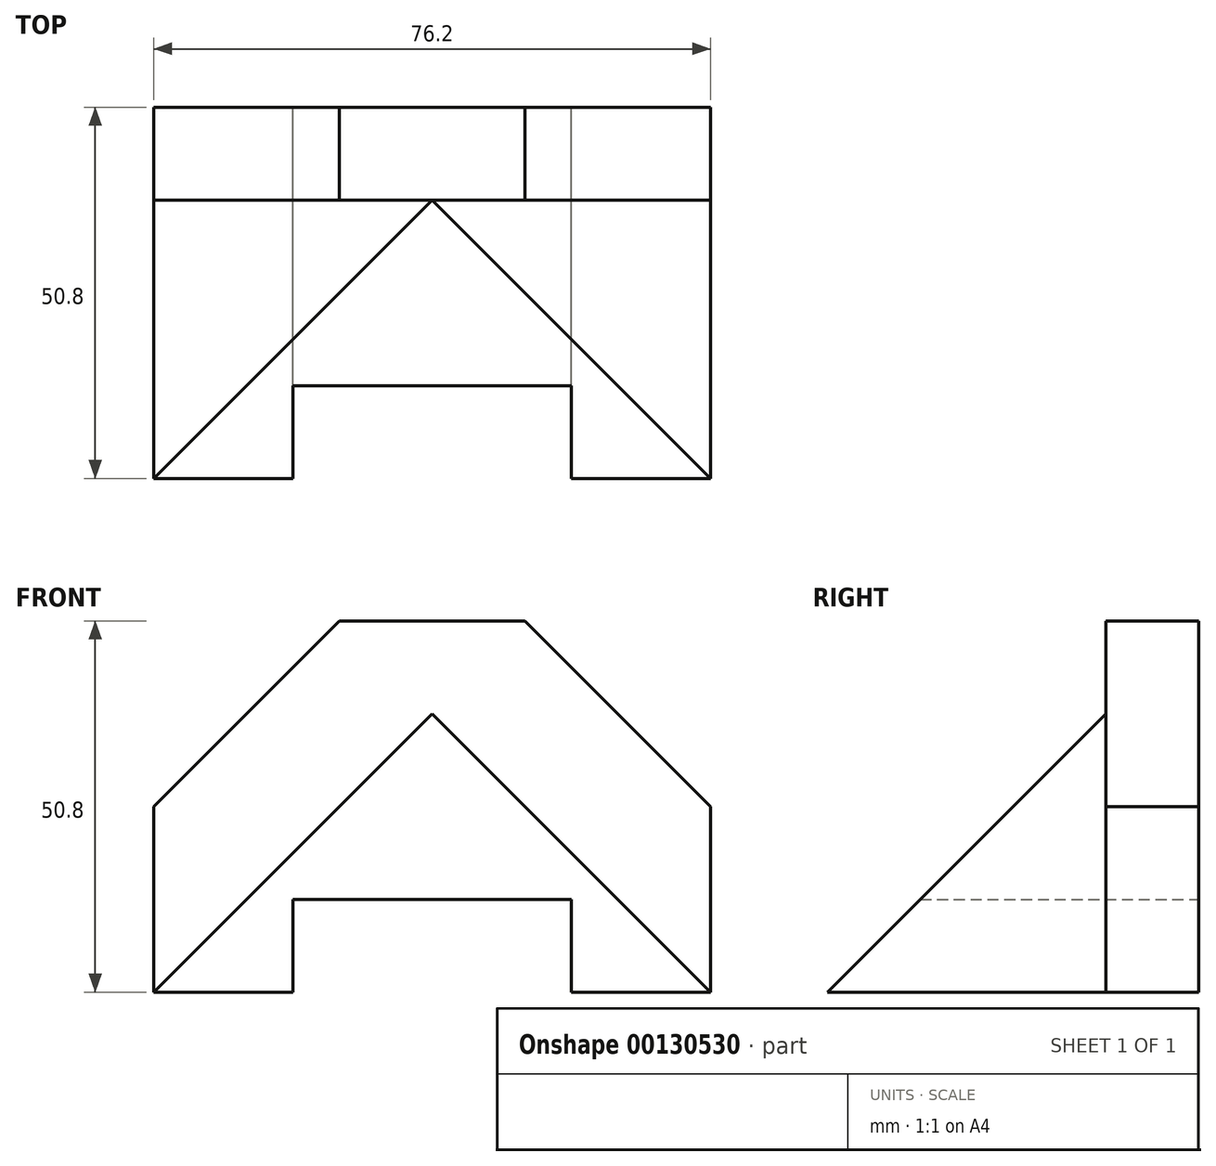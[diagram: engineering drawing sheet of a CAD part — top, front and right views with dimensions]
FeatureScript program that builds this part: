
annotation { "Feature Type Name" : "Feature", "Feature Type Description" : "" }
export const myFeature = defineFeature(function(context is Context, id is Id, definition is map)
    precondition{}
    {
        {
            var Q0;
            Q0=qCreatedBy(makeId("Front.planeOp"),FACE);
            var sketch = newSketch(context, id + "F0", { "sketchPlane" : qUnion([Q0])});
            skLineSegment(sketch, "E0", {"start": v(0, 0) * mm, "end": v(-38.1, 0) * mm});
            skLineSegment(sketch, "E1", {"start": v(-38.1, 0) * mm, "end": v(-38.1, 25.4) * mm});
            skLineSegment(sketch, "E2", {"start": v(-38.1, 25.4) * mm, "end": v(-12.7, 50.8) * mm});
            skLineSegment(sketch, "E3", {"start": v(-12.7, 50.8) * mm, "end": v(12.7, 50.8) * mm});
            skLineSegment(sketch, "E4", {"start": v(12.7, 50.8) * mm, "end": v(38.1, 25.4) * mm});
            skLineSegment(sketch, "E5", {"start": v(38.1, 25.4) * mm, "end": v(38.1, 0) * mm});
            skLineSegment(sketch, "E6", {"start": v(38.1, 0) * mm, "end": v(0, 0) * mm});
            skLineSegment(sketch, "E7", {"start": v(-38.1, 0) * mm, "end": v(0, 38.1) * mm});
            skLineSegment(sketch, "E8", {"start": v(0, 38.1) * mm, "end": v(38.1, 0) * mm});
            skPoint(sketch, "E9", {"position": v(0, 50.8) * mm});
            skSolve(sketch);
        }
        {
            var Q0;
            Q0=makeQuery(id+"F0.imprint","IMPRINT",FACE,{"disambiguationData":[TD([[makeQuery(id+"F0.imprint","IMPRINT",EDGE,{"derivedFrom":sQuery(id+"F0.wireOp",EDGE,"E0")}),-1.0]])]});
            extrude(context, id + "F1", {"entities" : qUnion([Q0]), "depth" : 50.8 * mm});
        }
        {
            var Q0;
            Q0=makeQuery(id+"F0.imprint","IMPRINT",FACE,{"disambiguationData":[TD([[makeQuery(id+"F0.imprint","IMPRINT",EDGE,{"derivedFrom":sQuery(id+"F0.wireOp",EDGE,"E1")}),-1.0]])]});
            extrude(context, id + "F2", {"entities" : qUnion([Q0]), "operationType" : NewBodyOperationType.ADD, "depth" : 12.7 * mm});
        }
        {
            var Q0;
            Q0=makeQuery(id+"F2.opExtrude","SWEPT_FACE",FACE,{"disambiguationData":[OSD([sQuery(id+"F0.wireOp",EDGE,"E5")])]});
            var sketch = newSketch(context, id + "F3", { "sketchPlane" : qUnion([Q0])});
            skLineSegment(sketch, "E10.0", {"start": v(-50.8, 38.1) * mm, "end": v(-50.8, 0) * mm});
            skLineSegment(sketch, "E10.1", {"start": v(-50.8, 38.1) * mm, "end": v(-12.7, 38.1) * mm});
            skLineSegment(sketch, "E11", {"start": v(-50.8, 0) * mm, "end": v(-12.7, 38.1) * mm});
            skSolve(sketch);
        }
        {
            var Q0;
            Q0 = qSketchRegion(id + "F3", true);
            extrude(context, id + "F4", {"entities" : qUnion([Q0]), "operationType" : NewBodyOperationType.REMOVE, "endBound" : BoundingType.THROUGH_ALL, "oppositeDirection" : true, "depth" : 25.4 * mm});
        }
        {
            var Q0;
            {var subQ0=sQuery(id+"F0.wireOp",EDGE,"E8");var subQ1=sQuery(id+"F0.wireOp",EDGE,"E7");Q0=makeQuery(id+"F2.boolean.opBoolean","MERGE",FACE,{"derivedFrom":[makeQuery(id+"F1.opExtrude","CAP_FACE",FACE,{"disambiguationData":[OSD([sQuery(id+"F0.wireOp",EDGE,"E0"),sQuery(id+"F0.wireOp",EDGE,"E6"),subQ1,subQ0])],"isStart":true}),makeQuery(id+"F2.opExtrude","CAP_FACE",FACE,{"disambiguationData":[OSD([sQuery(id+"F0.wireOp",EDGE,"E1"),sQuery(id+"F0.wireOp",EDGE,"E2"),sQuery(id+"F0.wireOp",EDGE,"E3"),sQuery(id+"F0.wireOp",EDGE,"E4"),sQuery(id+"F0.wireOp",EDGE,"E5"),subQ1,subQ0])],"isStart":true})]});}
            var sketch = newSketch(context, id + "F5", { "sketchPlane" : qUnion([Q0])});
            skLineSegment(sketch, "E12.bottom", {"start": v(-19.05, 0) * mm, "end": v(19.05, 0) * mm});
            skLineSegment(sketch, "E12.top", {"start": v(-19.05, 12.7) * mm, "end": v(19.05, 12.7) * mm});
            skLineSegment(sketch, "E12.left", {"start": v(-19.05, 0) * mm, "end": v(-19.05, 12.7) * mm});
            skLineSegment(sketch, "E12.right", {"start": v(19.05, 0) * mm, "end": v(19.05, 12.7) * mm});
            skSolve(sketch);
        }
        {
            var Q0;
            Q0 = qSketchRegion(id + "F5", true);
            extrude(context, id + "F6", {"entities" : qUnion([Q0]), "operationType" : NewBodyOperationType.REMOVE, "endBound" : BoundingType.THROUGH_ALL, "oppositeDirection" : true, "depth" : 25.4 * mm});
        }
    });
